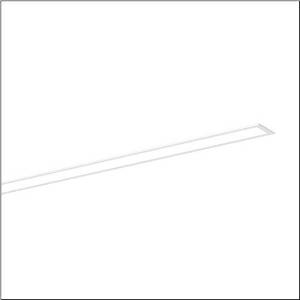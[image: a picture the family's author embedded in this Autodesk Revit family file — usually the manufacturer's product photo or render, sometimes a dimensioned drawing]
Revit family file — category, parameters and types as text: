
# Revit family: silica_21_51mx10dc35wb
name_source: partatom
category: Lighting Fixtures
units: mm (PartAtom-declared; Revit-internal decimal feet)

## family parameters
Cut with Voids When Loaded = No
Host = Face
Light Source = No
Part Type = Normal
Room Calculation Point = No
Round Connector Dimension = Use Diameter
Shared = No

## types (1)
- --- (1 x LED, 6000 lm, 42.6 W, 3000K)
    Apparent Load = 43 VA
    CIE Flux Codes = 48 79 96 100 100
    Color Rendering = 80
    Color Temperature = 3000K
    Default Elevation = 1800 mm
    Description = Silica 21, office luminaire, primary optical cover: cover, of PMMA, opal, light emission: direct distribution, primary light characteristic: symmetric, installation type: recessed, LED, rated luminous flux: 6.000lm, luminous efficacy: 141lm/W, light colour: 830, colour temperature: 3000K, control gear: DALI 2, with terminal, 3+2-pole, max. 2.5mm², mains connection: 220..240V, AC, 50/60Hz, rated input power: 42.6W, luminaire housing, of aluminium, traffic white (RAL 9016), length: 3.028mm, width: 79mm, height: 53mm, protection rating (complete): IP20, insulation class (complete): insulation class I (protective earthing), certification: CE, ENEC, VDE, permissible operating ambient temperature: 0..+35°C, standard: EN 50419, packaging unit: 1 piece
    Height = 0 mm  [stored 0 ft]
    Lamp = 1 x LED
    Lamp Light Flux = 6000 lm
    Lamp Power = 42.6 W
    Lamp count = 1
    Length = 3027 mm
    Luminous efficacy = 141 lm/W
    Manufacturer = Siteco
    ModVariant = No
    Model = 51MX10DC35WB
    Mounting Place = Ceiling
    Mounting Type = Recessed
    Number of Poles = 1
    OnlyDefault = Yes
    Power Factor = 1
    Product Name = Silica 21
    Product group = office luminaire | ceiling recessed
    ProductGroupID = 400
    Protection Class = Protection class I
    Protection Degree = IP 20
    RLX_Detail_Level = 1
    RLX_Emergency_Light_Flux = 0 lm
    RLX_Emergency_Type = 0
    RLX_Emergency_Type_DB = No
    RlxData = <blob elided: 21209 chars, md5=6f3f1468>
    Socket = socket
    Standby Power = 0 W
    System Light Flux = 6000 lm
    System Power = 43 W
    Type Comments = factory setting: luminous flux: 100 % | dim-lin: 254 | 233 mA
    Type Image = l_1335891.jpg
    URL = http://relux.com
    VarID = @adj_117763
    Voltage = 0 V
    Weight = 0.00 kg
    Width = 79 mm

note: [stored X ft] marks values corroborated as IEEE doubles in the binary element streams (Revit-internal decimal feet)

## geometry (parser evidence)
native form markers: Blend x4, Sweep x11
no freeform markers — native parametric forms only
